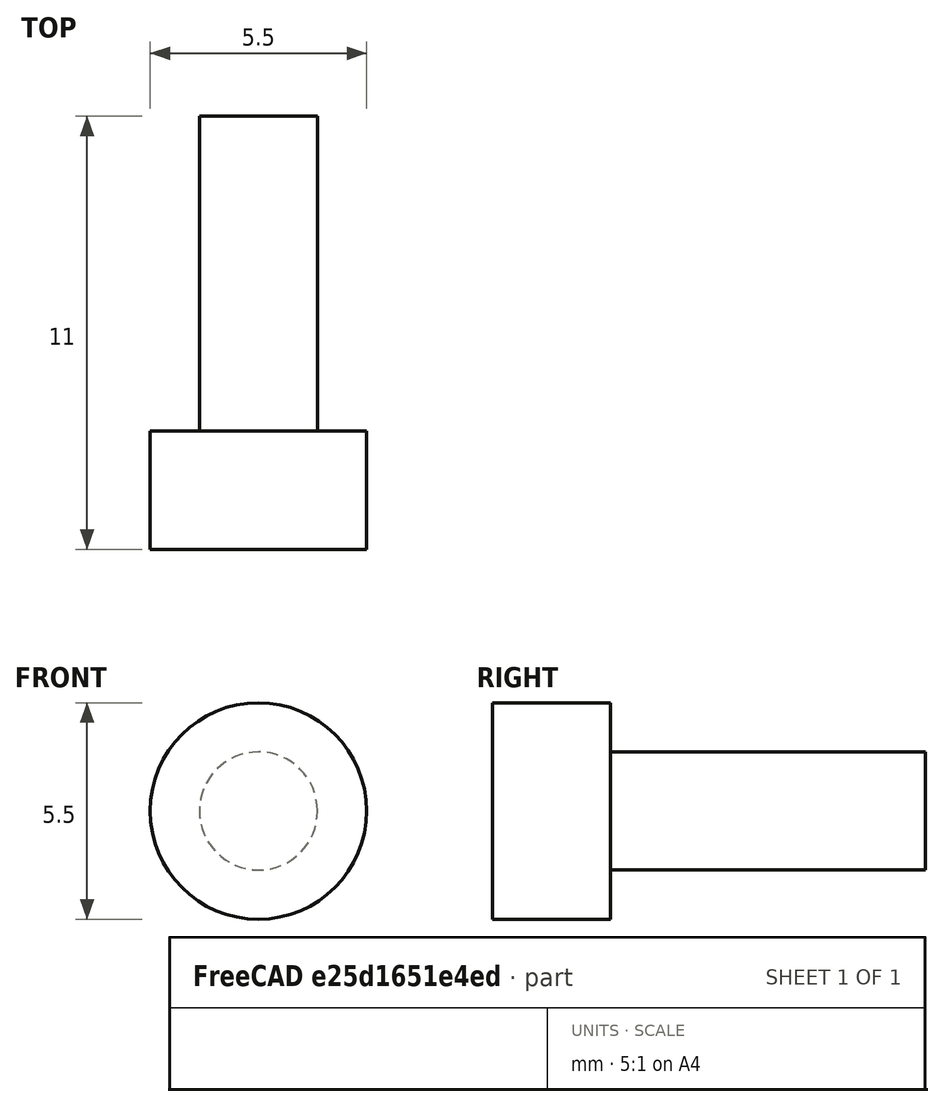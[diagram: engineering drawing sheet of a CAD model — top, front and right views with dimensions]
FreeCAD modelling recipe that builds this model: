
FCSTD DOCUMENT  (FreeCAD 1.0R39319 (Git))
Label: visM3L8
License: All rights reserved
LicenseURL: https://en.wikipedia.org/wiki/All_rights_reserved
objects: Sketcher::SketchObject×1, PartDesign::Revolution×1, PartDesign::Body×1
note: 6 computed .brp shape members not serialized (recipe doc carries the construction recipe); baked Part::Feature solids carry a one-line shape summary decoded from their .brp

FEATURE [Sketcher::SketchObject] Sketch
  ArcFitTolerance = 1e-06
  AttachmentSupport = -> [YZ_Plane]
  FullyConstrained = true
  MakeInternals = false
  MapMode = 5
  Placement = pos=(0,0,0) rot=(0.57735,0.57735,0.57735;2.0944rad)
  sketch-geometry (6):
    g0: LineSegment StartX=-3 StartY=0 StartZ=0 EndX=-3 EndY=2.75 EndZ=0
    g1: LineSegment StartX=-3 StartY=2.75 StartZ=0 EndX=0 EndY=2.75 EndZ=0
    g2: LineSegment StartX=0 StartY=2.75 StartZ=0 EndX=0 EndY=1.5 EndZ=0
    g3: LineSegment StartX=0 StartY=1.5 StartZ=0 EndX=8 EndY=1.5 EndZ=0
    g4: LineSegment StartX=8 StartY=0 StartZ=0 EndX=8 EndY=1.5 EndZ=0
    g5: LineSegment StartX=-3 StartY=0 StartZ=0 EndX=8 EndY=0 EndZ=0
  constraints (18):
    c: PointOnObject(g0,g-1)
    c: Vertical(g0)
    c: Coincident(g1,g0)
    c: PointOnObject(g1,g-2)
    c: Horizontal(g1)
    c: Coincident(g2,g1)
    c: PointOnObject(g2,g-2)
    c: Coincident(g3,g2)
    c: Horizontal(g3)
    c: PointOnObject(g4,g-1)
    c: Coincident(g5,g0)
    c: Coincident(g5,g4)
    c: Coincident(g4,g3)
    c: Perpendicular(g-1,g4)
    c: DistanceY(g0,g0) = 2.75
    c: DistanceX(g1,g1) = 3
    c: DistanceX(g3,g3) = 8
    c: DistanceY(g4,g4) = 1.5
FEATURE [PartDesign::Revolution] Revolution
  Angle = 360
  Angle2 = 60
  Axis = (1e-16,1,-1e-16)
  Base = (0,0,0)
  Placement = pos=(0,0,0) rot=(1,1,1;2.0944rad)
  Profile = -> Sketch
  ReferenceAxis = -> Y_Axis
  Refine = true
  Suppressed = false
  Type = 0
FEATURE [PartDesign::Body] Body  label="Corps"
  AllowCompound = false
  Group = -> [Sketch,Revolution]
  Origin = -> Origin
  Tip = -> Revolution
